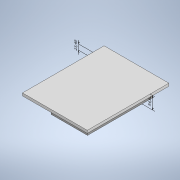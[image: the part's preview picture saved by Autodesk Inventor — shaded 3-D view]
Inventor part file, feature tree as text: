
AUTODESK INVENTOR PART (.ipt)
format: ipt  version: 2020 (Build 240168000, 168)  size: 346,112 bytes
history: native  units: mm
features: sketch x13, extrude x10, other x3, hole x3
ambient origin geometry x8: Origin, YZ Plane, XZ Plane, XY Plane, X Axis, Y Axis, Z Axis, Center Point
bodies: Solid1 (feature_tree)
feature tree (29):
  other  "Annotations"
  sketch  "Sketch1"  dims[d0=354.0mm d1=281.0mm]
  extrude  "Extrusion1"  Depth=281.0mm
  extrude  "Extrusion2"  Depth=12.0mm TaperAngle=0.0deg
  extrude  "Extrusion3"  Depth=31.2mm TaperAngle=0.0deg
  extrude  "Extrusion4"  Depth=18.0mm
  extrude  "Extrusion5"  Depth=10.0mm
  hole  "Hole4"  [1 undecoded]
  hole  "Hole5"  [1 undecoded]
  hole  "Hole6"  [1 undecoded]
  extrude  "Extrusion6"  Depth=8.0mm
  extrude  "Extrusion7"  Depth=10.0mm
  extrude  "Extrusion8"  Depth=8.0mm
  extrude  "Extrusion9"  Depth=54.6mm
  extrude  "Extrusion11"  Depth=54.6mm
  sketch  "Sketch2"  dims[d2=11.4mm d3=0.0mm d6=12.0mm d7=0.0mm]
  sketch  "Sketch7"  dims[d62=158.0mm d65=31.2mm d66=0.0mm]
  sketch  "Sketch8"  dims[d67=116.0mm d68=18.0mm]
  sketch  "Sketch9"  dims[d69=6.3mm d70=10.0mm]
  sketch  "Sketch10"  dims[d71=1.0mm d72=0.0mm d73=5.5mm]
  sketch  "Sketch11"  dims[d74=57.85mm d75=11.75mm]
  sketch  "Sketch12"  dims[d76=57.85mm d77=1.0mm d78=0.0mm]
  sketch  "Sketch13"  dims[d79=7.0mm d80=6.0mm d81=4.0mm d82=2.0mm d83=90.0deg d84=8.0mm d85=20.594885mm d86=20.8mm]
  sketch  "Sketch14"  dims[d87=7.0mm d88=20.0mm d90=240.1mm d91=10.0mm d93=10.0mm]
  sketch  "Sketch15"  dims[d95=21.1mm]
  sketch  "Sketch16"  dims[d96=7.0mm d97=6.0mm d98=4.0mm d99=2.0mm d100=90.0deg d101=8.0mm d102=20.594885mm d103=141.0mm]
  sketch  "Sketch20"  dims[d104=7.0mm d105=7.0mm d106=6.0mm d107=4.0mm d108=2.0mm d109=90.0deg d110=8.0mm d111=20.594885mm d112=103.35mm d113=33.8mm d114=20.0mm d116=74.5mm d117=20.0mm d119=74.5mm d122=59.0mm d123=27.5mm d124=22.0mm d125=10.0mm d126=0.0mm d128=6.2mm d129=17.0mm d130=19.4mm d133=7.0mm d134=1.5mm d135=0.0mm d136=7.0mm d137=6.2mm d138=15.0mm d139=1.5mm d140=0.0mm d141=19.4mm d142=10.5mm d144=5.0mm d145=20.0mm d147=24.5mm d148=10.0mm d150=10.0mm d152=5.0mm d153=0.0mm d185=160.5mm d189=4.0mm d190=8.5mm d191=8.5mm d192=8.5mm d193=8.5mm d194=8.5mm d195=8.5mm d196=8.5mm d197=8.5mm d204=36.0mm d205=36.0mm d206=35.0mm d207=16.5mm d208=16.5mm d209=16.5mm d210=14.7mm d211=8.5mm d212=354.0mm d213=177.0mm d214=8.5mm d215=177.0mm d216=8.5mm d217=281.0mm d218=140.5mm d220=140.5mm d221=8.5mm d222=140.0mm d223=19.0mm d224=12.25mm d225=19.0mm d226=16.25mm d227=8.0mm d228=21.0mm d229=6.5mm d230=6.5mm d231=6.5mm d232=21.0mm d233=240.0mm d234=120.0mm d235=10.0mm d236=0.0mm d198=8.999256mm d199=1.322263mm d200=23.4mm d201=8.3798mm d202=5.324182mm d203=54.6mm]
  other  "Linear Dimension 1"
  other  "Linear Dimension 2"
note: 3 required parameter values undecoded (feature->parameter linkage not recoverable at this tier; creation-order binding heuristic only, values carry confidence <= 0.55)
